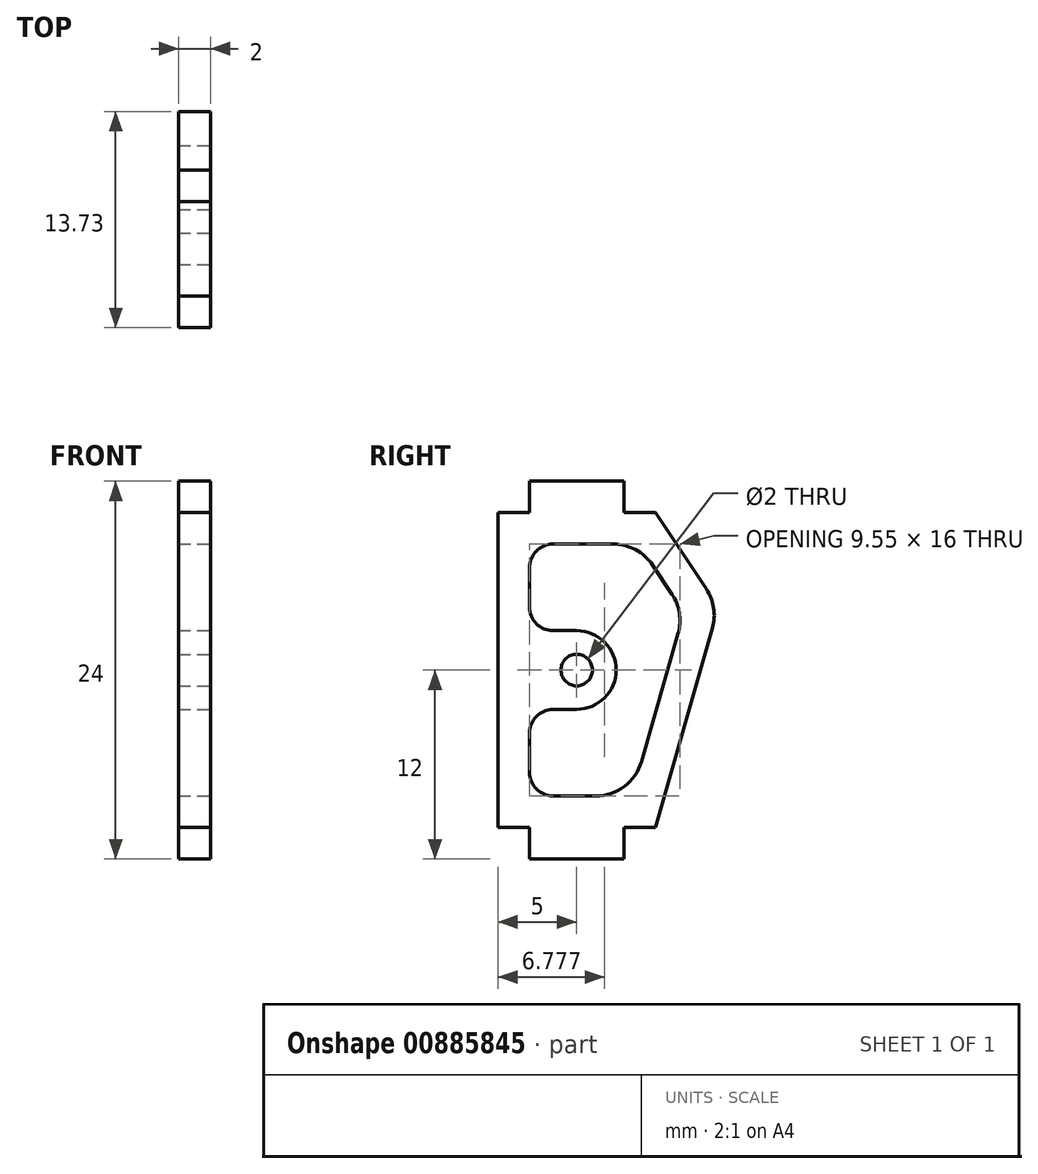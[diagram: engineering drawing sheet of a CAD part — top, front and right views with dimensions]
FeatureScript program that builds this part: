
annotation { "Feature Type Name" : "Feature", "Feature Type Description" : "" }
export const myFeature = defineFeature(function(context is Context, id is Id, definition is map)
    precondition{}
    {
        {
            var Q0;
            Q0=qCreatedBy(makeId("Right.planeOp"),FACE);
            var sketch = newSketch(context, id + "F0", { "sketchPlane" : qUnion([Q0])});
            skLineSegment(sketch, "E0", {"start": v(-3, -2) * mm, "end": v(3, -2) * mm});
            skLineSegment(sketch, "E1", {"start": v(3, -2) * mm, "end": v(3, 0) * mm});
            skLineSegment(sketch, "E2", {"start": v(3, 0) * mm, "end": v(5, 0) * mm});
            skLineSegment(sketch, "E3", {"start": v(5, 0) * mm, "end": v(5, 20) * mm});
            skLineSegment(sketch, "E4", {"start": v(5, 20) * mm, "end": v(3, 20) * mm});
            skLineSegment(sketch, "E5", {"start": v(3, 20) * mm, "end": v(3, 22) * mm});
            skLineSegment(sketch, "E6", {"start": v(3, 22) * mm, "end": v(-3, 22) * mm});
            skLineSegment(sketch, "E7", {"start": v(-3, 22) * mm, "end": v(-3, 20) * mm});
            skLineSegment(sketch, "E8", {"start": v(-3, 20) * mm, "end": v(-5, 20) * mm});
            skLineSegment(sketch, "E9", {"start": v(-5, 20) * mm, "end": v(-5, 0) * mm});
            skLineSegment(sketch, "E10", {"start": v(-5, 0) * mm, "end": v(-3, 0) * mm});
            skLineSegment(sketch, "E11", {"start": v(-3, 0) * mm, "end": v(-3, -2) * mm});
            skSolve(sketch);
        }
        {
            var Q0;
            Q0 = qSketchRegion(id + "F0", true);
            extrude(context, id + "F1", {"entities" : qUnion([Q0]), "depth" : 2 * mm, "offsetDistance" : 25 * mm});
        }
        {
            var Q0;
            Q0=makeQuery(id+"F1.opExtrude","CAP_FACE",FACE,{"disambiguationData":[OSD([sQuery(id+"F0.wireOp",EDGE,"E0"),sQuery(id+"F0.wireOp",EDGE,"E1"),sQuery(id+"F0.wireOp",EDGE,"E2"),sQuery(id+"F0.wireOp",EDGE,"E3"),sQuery(id+"F0.wireOp",EDGE,"E4"),sQuery(id+"F0.wireOp",EDGE,"E5"),sQuery(id+"F0.wireOp",EDGE,"E6"),sQuery(id+"F0.wireOp",EDGE,"E7"),sQuery(id+"F0.wireOp",EDGE,"E8"),sQuery(id+"F0.wireOp",EDGE,"E9"),sQuery(id+"F0.wireOp",EDGE,"E10"),sQuery(id+"F0.wireOp",EDGE,"E11")])],"isStart":false});
            var sketch = newSketch(context, id + "F2", { "sketchPlane" : qUnion([Q0])});
            skLineSegment(sketch, "E12", {"start": v(5, 0) * mm, "end": v(8.62, 12.67) * mm});
            skLineSegment(sketch, "E13", {"start": v(8.23, 15.15) * mm, "end": v(5, 20) * mm});
            skLineSegment(sketch, "E14", {"start": v(5, 20) * mm, "end": v(3, 20) * mm});
            skLineSegment(sketch, "E15", {"start": v(3, 20) * mm, "end": v(3, 0) * mm});
            skLineSegment(sketch, "E16", {"start": v(3, 0) * mm, "end": v(5, 0) * mm});
            skPoint(sketch, "E17.visualSharp", {"position": v(9, 14) * mm});
            skArc(sketch, "E17.filletArc", {"start": v(8.62, 12.67) * mm, "mid": v(8.7, 13.95) * mm, "end": v(8.23, 15.15) * mm});
            skSolve(sketch);
        }
        {
            var Q0;
            Q0 = qSketchRegion(id + "F2", true);
            var Q1;
            Q1=makeQuery(id+"F1.opExtrude","CAP_FACE",FACE,{"disambiguationData":[OSD([sQuery(id+"F0.wireOp",EDGE,"E0"),sQuery(id+"F0.wireOp",EDGE,"E1"),sQuery(id+"F0.wireOp",EDGE,"E2"),sQuery(id+"F0.wireOp",EDGE,"E3"),sQuery(id+"F0.wireOp",EDGE,"E4"),sQuery(id+"F0.wireOp",EDGE,"E5"),sQuery(id+"F0.wireOp",EDGE,"E6"),sQuery(id+"F0.wireOp",EDGE,"E7"),sQuery(id+"F0.wireOp",EDGE,"E8"),sQuery(id+"F0.wireOp",EDGE,"E9"),sQuery(id+"F0.wireOp",EDGE,"E10"),sQuery(id+"F0.wireOp",EDGE,"E11")])],"isStart":true});
            extrude(context, id + "F3", {"entities" : qUnion([Q0]), "operationType" : NewBodyOperationType.ADD, "endBound" : BoundingType.UP_TO_SURFACE, "oppositeDirection" : true, "depth" : 25 * mm, "endBoundEntityFace" : qUnion([Q1]), "offsetDistance" : 25 * mm});
        }
        {
            var Q0;
            Q0=makeQuery(id+"F3.boolean.opBoolean","MERGE",FACE,{"derivedFrom":[makeQuery(id+"F1.opExtrude","CAP_FACE",FACE,{"disambiguationData":[OSD([sQuery(id+"F0.wireOp",EDGE,"E0"),sQuery(id+"F0.wireOp",EDGE,"E1"),sQuery(id+"F0.wireOp",EDGE,"E2"),sQuery(id+"F0.wireOp",EDGE,"E3"),sQuery(id+"F0.wireOp",EDGE,"E4"),sQuery(id+"F0.wireOp",EDGE,"E5"),sQuery(id+"F0.wireOp",EDGE,"E6"),sQuery(id+"F0.wireOp",EDGE,"E7"),sQuery(id+"F0.wireOp",EDGE,"E8"),sQuery(id+"F0.wireOp",EDGE,"E9"),sQuery(id+"F0.wireOp",EDGE,"E10"),sQuery(id+"F0.wireOp",EDGE,"E11")])],"isStart":false}),makeQuery(id+"F3.opExtrude","CAP_FACE",FACE,{"disambiguationData":[OSD([sQuery(id+"F2.wireOp",EDGE,"E12"),sQuery(id+"F2.wireOp",EDGE,"E13"),sQuery(id+"F2.wireOp",EDGE,"E14"),sQuery(id+"F2.wireOp",EDGE,"E15"),sQuery(id+"F2.wireOp",EDGE,"E16"),sQuery(id+"F2.wireOp",EDGE,"E17.filletArc")])],"isStart":true})]});
            var sketch = newSketch(context, id + "F4", { "sketchPlane" : qUnion([Q0])});
            skCircle(sketch, "E18", {"center": v(0, 10) * mm, "radius": 1 * mm});
            skPoint(sketch, "E18.centerSnap0", {"position": v(0, 22) * mm});
            skSolve(sketch);
        }
        {
            var Q0;
            Q0 = qSketchRegion(id + "F4", true);
            extrude(context, id + "F5", {"entities" : qUnion([Q0]), "operationType" : NewBodyOperationType.REMOVE, "endBound" : BoundingType.THROUGH_ALL, "oppositeDirection" : true, "depth" : 25 * mm, "offsetDistance" : 25 * mm});
        }
        {
            var Q0;
            Q0=makeQuery(id+"F3.boolean.opBoolean","MERGE",FACE,{"derivedFrom":[makeQuery(id+"F1.opExtrude","CAP_FACE",FACE,{"disambiguationData":[OSD([sQuery(id+"F0.wireOp",EDGE,"E0"),sQuery(id+"F0.wireOp",EDGE,"E1"),sQuery(id+"F0.wireOp",EDGE,"E2"),sQuery(id+"F0.wireOp",EDGE,"E3"),sQuery(id+"F0.wireOp",EDGE,"E4"),sQuery(id+"F0.wireOp",EDGE,"E5"),sQuery(id+"F0.wireOp",EDGE,"E6"),sQuery(id+"F0.wireOp",EDGE,"E7"),sQuery(id+"F0.wireOp",EDGE,"E8"),sQuery(id+"F0.wireOp",EDGE,"E9"),sQuery(id+"F0.wireOp",EDGE,"E10"),sQuery(id+"F0.wireOp",EDGE,"E11")])],"isStart":false}),makeQuery(id+"F3.opExtrude","CAP_FACE",FACE,{"disambiguationData":[OSD([sQuery(id+"F2.wireOp",EDGE,"E12"),sQuery(id+"F2.wireOp",EDGE,"E13"),sQuery(id+"F2.wireOp",EDGE,"E14"),sQuery(id+"F2.wireOp",EDGE,"E15"),sQuery(id+"F2.wireOp",EDGE,"E16"),sQuery(id+"F2.wireOp",EDGE,"E17.filletArc")])],"isStart":true})]});
            var sketch = newSketch(context, id + "F6", { "sketchPlane" : qUnion([Q0])});
            skLineSegment(sketch, "E19", {"start": v(4.11, 4.18) * mm, "end": v(6.44, 12.33) * mm});
            skLineSegment(sketch, "E20", {"start": v(6.05, 14.81) * mm, "end": v(4.82, 16.66) * mm});
            skLineSegment(sketch, "E21", {"start": v(2.32, 18) * mm, "end": v(-1.5, 18) * mm});
            skLineSegment(sketch, "E22", {"start": v(-3, 16.5) * mm, "end": v(-3, 14) * mm});
            skLineSegment(sketch, "E23", {"start": v(-1.5, 12.5) * mm, "end": v(0, 12.5) * mm});
            skLineSegment(sketch, "E24", {"start": v(1.23, 2) * mm, "end": v(-1.5, 2) * mm});
            skLineSegment(sketch, "E25", {"start": v(-3, 3.5) * mm, "end": v(-3, 6) * mm});
            skLineSegment(sketch, "E26", {"start": v(-1.5, 7.5) * mm, "end": v(0, 7.5) * mm});
            skArc(sketch, "E27", {"start": v(0, 12.5) * mm, "mid": v(2.5, 10) * mm, "end": v(0, 7.5) * mm});
            skPoint(sketch, "E28.visualSharp", {"position": v(6.82, 13.66) * mm});
            skArc(sketch, "E28.filletArc", {"start": v(6.44, 12.33) * mm, "mid": v(6.52, 13.61) * mm, "end": v(6.05, 14.81) * mm});
            skPoint(sketch, "E29.visualSharp", {"position": v(3.93, 18) * mm});
            skArc(sketch, "E29.filletArc", {"start": v(4.82, 16.66) * mm, "mid": v(3.74, 17.65) * mm, "end": v(2.32, 18) * mm});
            skPoint(sketch, "E30.visualSharp", {"position": v(-3, 18) * mm});
            skArc(sketch, "E30.filletArc", {"start": v(-1.5, 18) * mm, "mid": v(-2.56, 17.56) * mm, "end": v(-3, 16.5) * mm});
            skPoint(sketch, "E31.visualSharp", {"position": v(-3, 12.5) * mm});
            skArc(sketch, "E31.filletArc", {"start": v(-3, 14) * mm, "mid": v(-2.56, 12.94) * mm, "end": v(-1.5, 12.5) * mm});
            skPoint(sketch, "E32.visualSharp", {"position": v(-3, 7.5) * mm});
            skArc(sketch, "E32.filletArc", {"start": v(-1.5, 7.5) * mm, "mid": v(-2.56, 7.06) * mm, "end": v(-3, 6) * mm});
            skPoint(sketch, "E33.visualSharp", {"position": v(-3, 2) * mm});
            skArc(sketch, "E33.filletArc", {"start": v(-3, 3.5) * mm, "mid": v(-2.56, 2.44) * mm, "end": v(-1.5, 2) * mm});
            skPoint(sketch, "E34.visualSharp", {"position": v(3.5, 2) * mm});
            skArc(sketch, "E34.filletArc", {"start": v(1.23, 2) * mm, "mid": v(3.04, 2.6) * mm, "end": v(4.11, 4.18) * mm});
            skSolve(sketch);
        }
        {
            var Q0;
            Q0 = qSketchRegion(id + "F6", true);
            extrude(context, id + "F7", {"entities" : qUnion([Q0]), "operationType" : NewBodyOperationType.REMOVE, "endBound" : BoundingType.THROUGH_ALL, "oppositeDirection" : true, "depth" : 25 * mm, "offsetDistance" : 25 * mm});
        }
    });
